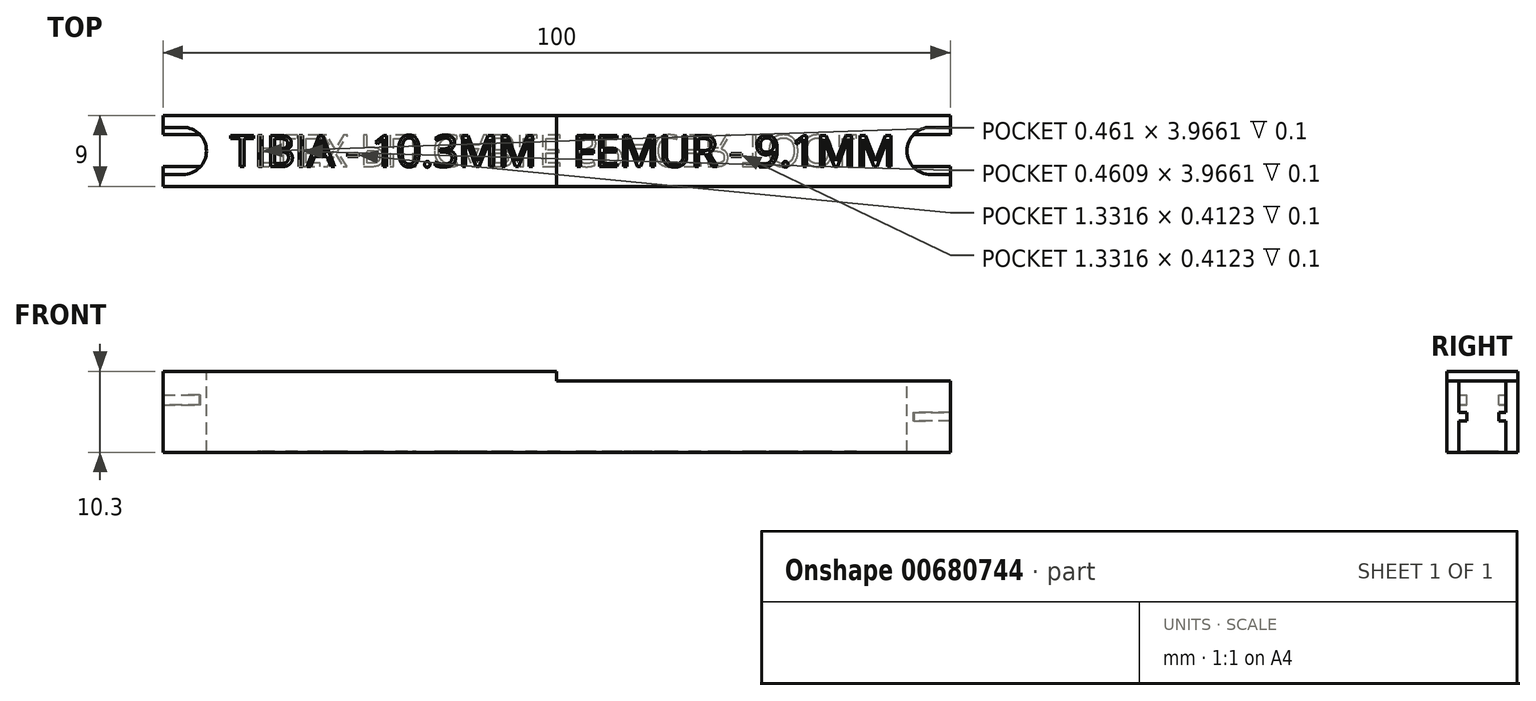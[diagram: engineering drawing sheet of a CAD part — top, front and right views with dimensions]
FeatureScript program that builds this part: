
annotation { "Feature Type Name" : "Feature", "Feature Type Description" : "" }
export const myFeature = defineFeature(function(context is Context, id is Id, definition is map)
    precondition{}
    {
        {
            var Q0;
            Q0=qCreatedBy(makeId("Front.planeOp"),FACE);
            var sketch = newSketch(context, id + "F0", { "sketchPlane" : qUnion([Q0])});
            skLineSegment(sketch, "E0.bottom", {"start": v(0, 0) * mm, "end": v(50, 0) * mm});
            skLineSegment(sketch, "E0.top", {"start": v(0, 10.3) * mm, "end": v(50, 10.3) * mm});
            skLineSegment(sketch, "E0.left", {"start": v(0, 0) * mm, "end": v(0, 10.3) * mm});
            skLineSegment(sketch, "E0.right", {"start": v(50, 9.1) * mm, "end": v(50, 10.3) * mm});
            skLineSegment(sketch, "E1.bottom", {"start": v(50, 0) * mm, "end": v(100, 0) * mm});
            skLineSegment(sketch, "E1.top", {"start": v(50, 9.1) * mm, "end": v(100, 9.1) * mm});
            skLineSegment(sketch, "E1.right", {"start": v(100, 0) * mm, "end": v(100, 9.1) * mm});
            skSolve(sketch);
        }
        {
            var Q0;
            Q0 = qSketchRegion(id + "F0", true);
            extrude(context, id + "F1", {"entities" : qUnion([Q0]), "depth" : 9 * mm, "offsetDistance" : 25 * mm});
        }
        {
            var Q0;
            Q0=makeQuery(id+"F1.opExtrude","SWEPT_FACE",FACE,{"disambiguationData":[OSD([sQuery(id+"F0.wireOp",EDGE,"E0.top")])]});
            var sketch = newSketch(context, id + "F2", { "sketchPlane" : qUnion([Q0])});
            skLineSegment(sketch, "E2.top", {"start": v(0, -1.5) * mm, "end": v(2.5, -1.5) * mm});
            skLineSegment(sketch, "E2.left", {"start": v(0, -4.5) * mm, "end": v(0, -1.5) * mm});
            skLineSegment(sketch, "E3.top", {"start": v(0, -7.5) * mm, "end": v(2.5, -7.5) * mm});
            skLineSegment(sketch, "E3.left", {"start": v(0, -4.5) * mm, "end": v(0, -7.5) * mm});
            skArc(sketch, "E4", {"start": v(2.5, -7.5) * mm, "mid": v(5.5, -4.5) * mm, "end": v(2.5, -1.5) * mm});
            skSolve(sketch);
        }
        {
            var Q0;
            Q0=makeQuery(id+"F1.opExtrude","SWEPT_FACE",FACE,{"disambiguationData":[OSD([sQuery(id+"F0.wireOp",EDGE,"E1.top")])]});
            var sketch = newSketch(context, id + "F3", { "sketchPlane" : qUnion([Q0])});
            skLineSegment(sketch, "E5.top", {"start": v(100, -1.5) * mm, "end": v(97.5, -1.5) * mm});
            skLineSegment(sketch, "E5.left", {"start": v(100, -4.5) * mm, "end": v(100, -1.5) * mm});
            skLineSegment(sketch, "E6.top", {"start": v(100, -7.5) * mm, "end": v(97.5, -7.5) * mm});
            skLineSegment(sketch, "E6.left", {"start": v(100, -4.5) * mm, "end": v(100, -7.5) * mm});
            skArc(sketch, "E7", {"start": v(97.5, -1.5) * mm, "mid": v(94.5, -4.5) * mm, "end": v(97.5, -7.5) * mm});
            skSolve(sketch);
        }
        {
            var Q0;
            Q0 = qSketchRegion(id + "F2", true);
            extrude(context, id + "F4", {"entities" : qUnion([Q0]), "operationType" : NewBodyOperationType.REMOVE, "oppositeDirection" : true, "depth" : 3 * mm, "offsetDistance" : 25 * mm});
        }
        {
            var Q0;
            Q0 = qSketchRegion(id + "F3", true);
            extrude(context, id + "F5", {"entities" : qUnion([Q0]), "operationType" : NewBodyOperationType.REMOVE, "oppositeDirection" : true, "depth" : 4 * mm, "offsetDistance" : 25 * mm});
        }
        {
            var Q0;
            Q0=makeQuery(id+"F1.opExtrude","SWEPT_FACE",FACE,{"disambiguationData":[OSD([sQuery(id+"F0.wireOp",EDGE,"E0.bottom"),sQuery(id+"F0.wireOp",EDGE,"E1.bottom")])]});
            var sketch = newSketch(context, id + "F6", { "sketchPlane" : qUnion([Q0])});
            skLineSegment(sketch, "E8.top", {"start": v(0, 7.5) * mm, "end": v(2.5, 7.5) * mm});
            skLineSegment(sketch, "E8.left", {"start": v(0, 4.5) * mm, "end": v(0, 7.5) * mm});
            skLineSegment(sketch, "E9.top", {"start": v(0, 1.5) * mm, "end": v(2.5, 1.5) * mm});
            skLineSegment(sketch, "E9.left", {"start": v(0, 4.5) * mm, "end": v(0, 1.5) * mm});
            skArc(sketch, "E10", {"start": v(2.5, 1.5) * mm, "mid": v(5.5, 4.5) * mm, "end": v(2.5, 7.5) * mm});
            skSolve(sketch);
        }
        {
            var Q0;
            Q0 = qSketchRegion(id + "F6", true);
            extrude(context, id + "F7", {"entities" : qUnion([Q0]), "operationType" : NewBodyOperationType.REMOVE, "oppositeDirection" : true, "depth" : 6 * mm, "offsetDistance" : 25 * mm});
        }
        {
            var Q0;
            Q0=makeQuery(id+"F1.opExtrude","SWEPT_FACE",FACE,{"disambiguationData":[OSD([sQuery(id+"F0.wireOp",EDGE,"E0.bottom"),sQuery(id+"F0.wireOp",EDGE,"E1.bottom")])]});
            var sketch = newSketch(context, id + "F8", { "sketchPlane" : qUnion([Q0])});
            skLineSegment(sketch, "E11.top", {"start": v(100, 7.5) * mm, "end": v(97.5, 7.5) * mm});
            skLineSegment(sketch, "E11.left", {"start": v(100, 4.5) * mm, "end": v(100, 7.5) * mm});
            skLineSegment(sketch, "E12.top", {"start": v(100, 1.5) * mm, "end": v(97.5, 1.5) * mm});
            skLineSegment(sketch, "E12.left", {"start": v(100, 4.5) * mm, "end": v(100, 1.5) * mm});
            skArc(sketch, "E13", {"start": v(97.5, 7.5) * mm, "mid": v(94.5, 4.5) * mm, "end": v(97.5, 1.5) * mm});
            skSolve(sketch);
        }
        {
            var Q0;
            Q0 = qSketchRegion(id + "F8", true);
            extrude(context, id + "F9", {"entities" : qUnion([Q0]), "operationType" : NewBodyOperationType.REMOVE, "oppositeDirection" : true, "depth" : 4 * mm, "offsetDistance" : 25 * mm});
        }
        {
            var Q0;
            Q0=makeQuery(id+"F4.boolean.opBoolean","COPY",FACE,{"derivedFrom":makeQuery(id+"F4.opExtrude","CAP_FACE",FACE,{"disambiguationData":[OSD([sQuery(id+"F2.wireOp",EDGE,"E2.top"),sQuery(id+"F2.wireOp",EDGE,"E2.left"),sQuery(id+"F2.wireOp",EDGE,"E3.top"),sQuery(id+"F2.wireOp",EDGE,"E3.left"),sQuery(id+"F2.wireOp",EDGE,"E4")])],"isStart":false})});
            var sketch = newSketch(context, id + "F10", { "sketchPlane" : qUnion([Q0])});
            skLineSegment(sketch, "E14", {"start": v(0, -6.5) * mm, "end": v(4.74, -6.5) * mm});
            skLineSegment(sketch, "E15", {"start": v(0, -2.4) * mm, "end": v(4.64, -2.4) * mm});
            skLineSegment(sketch, "E16", {"start": v(0, -2.4) * mm, "end": v(0, -6.5) * mm});
            skArc(sketch, "E17", {"start": v(4.74, -6.5) * mm, "mid": v(5.5, -4.43) * mm, "end": v(4.64, -2.4) * mm});
            skSolve(sketch);
        }
        {
            var Q0;
            Q0 = qSketchRegion(id + "F10", true);
            extrude(context, id + "F11", {"entities" : qUnion([Q0]), "operationType" : NewBodyOperationType.REMOVE, "oppositeDirection" : true, "depth" : 2 * mm, "offsetDistance" : 25 * mm});
        }
        {
            var Q0;
            Q0=makeQuery(id+"F9.boolean.opBoolean","COPY",FACE,{"derivedFrom":makeQuery(id+"F9.opExtrude","CAP_FACE",FACE,{"disambiguationData":[OSD([sQuery(id+"F8.wireOp",EDGE,"E11.top"),sQuery(id+"F8.wireOp",EDGE,"E11.left"),sQuery(id+"F8.wireOp",EDGE,"E12.top"),sQuery(id+"F8.wireOp",EDGE,"E12.left"),sQuery(id+"F8.wireOp",EDGE,"E13")])],"isStart":false})});
            var sketch = newSketch(context, id + "F12", { "sketchPlane" : qUnion([Q0])});
            skLineSegment(sketch, "E18", {"start": v(100, 6.5) * mm, "end": v(95.26, 6.5) * mm});
            skLineSegment(sketch, "E19", {"start": v(100, 2.4) * mm, "end": v(95.36, 2.4) * mm});
            skLineSegment(sketch, "E20", {"start": v(100, 2.4) * mm, "end": v(100, 6.5) * mm});
            skArc(sketch, "E21", {"start": v(95.26, 6.5) * mm, "mid": v(94.5, 4.43) * mm, "end": v(95.36, 2.4) * mm});
            skSolve(sketch);
        }
        {
            var Q0;
            Q0 = qSketchRegion(id + "F12", true);
            extrude(context, id + "F13", {"entities" : qUnion([Q0]), "operationType" : NewBodyOperationType.REMOVE, "oppositeDirection" : true, "depth" : 2 * mm, "offsetDistance" : 25 * mm});
        }
        {
            var Q0;
            Q0=makeQuery(id+"F1.opExtrude","SWEPT_FACE",FACE,{"disambiguationData":[OSD([sQuery(id+"F0.wireOp",EDGE,"E0.top")])]});
            var sketch = newSketch(context, id + "F14", { "sketchPlane" : qUnion([Q0])});
            skLineSegment(sketch, "E22", {"start": v(8.5, 0) * mm, "end": v(8.5, -9) * mm, "construction": true});
            skLineSegment(sketch, "E23", {"start": v(8.5, -2.5) * mm, "end": v(47.32, -2.5) * mm, "construction": true});
            skLineSegment(sketch, "E24", {"start": v(8.5, -6.5) * mm, "end": v(47.32, -6.5) * mm, "construction": true});
            skText(sketch, "E25", { "text": "TIBIA - 10.3MM", "fontName": "OpenSans-Regular.ttf"});
            const initialGuessF14  = {"E25": [0.0085, -0.0065, 1, 0, 0.004]};
            skSetInitialGuess(sketch, initialGuessF14);
            skSolve(sketch);
        }
        {
            var Q0;
            Q0=makeQuery(id+"F1.opExtrude","SWEPT_FACE",FACE,{"disambiguationData":[OSD([sQuery(id+"F0.wireOp",EDGE,"E1.top")])]});
            var sketch = newSketch(context, id + "F15", { "sketchPlane" : qUnion([Q0])});
            skLineSegment(sketch, "E26", {"start": v(53.7, -2.5) * mm, "end": v(92.8, -2.5) * mm, "construction": true});
            skLineSegment(sketch, "E27", {"start": v(53.7, -6.5) * mm, "end": v(92.8, -6.5) * mm, "construction": true});
            skText(sketch, "E28", { "text": "FEMUR - 9.1MM", "fontName": "OpenSans-Regular.ttf"});
            const initialGuessF15  = {"E28": [0.052, -0.0065, 1, 0, 0.004]};
            skSetInitialGuess(sketch, initialGuessF15);
            skSolve(sketch);
        }
        {
            var Q0;
            Q0 = qSketchRegion(id + "F14", true);
            extrude(context, id + "F16", {"entities" : qUnion([Q0]), "operationType" : NewBodyOperationType.REMOVE, "oppositeDirection" : true, "depth" : 0.1 * mm, "offsetDistance" : 25 * mm});
        }
        {
            var Q0;
            Q0 = qSketchRegion(id + "F15", true);
            extrude(context, id + "F17", {"entities" : qUnion([Q0]), "operationType" : NewBodyOperationType.REMOVE, "oppositeDirection" : true, "depth" : 0.1 * mm, "offsetDistance" : 25 * mm});
        }
        {
            var Q0;
            Q0=makeQuery(id+"F1.opExtrude","SWEPT_FACE",FACE,{"disambiguationData":[OSD([sQuery(id+"F0.wireOp",EDGE,"E0.bottom"),sQuery(id+"F0.wireOp",EDGE,"E1.bottom")])]});
            var sketch = newSketch(context, id + "F18", { "sketchPlane" : qUnion([Q0])});
            skLineSegment(sketch, "E29", {"start": v(7.24, 6.5) * mm, "end": v(93.12, 6.5) * mm, "construction": true});
            skLineSegment(sketch, "E30", {"start": v(7.24, 2.5) * mm, "end": v(93.22, 2.5) * mm, "construction": true});
            skLineSegment(sketch, "E31", {"start": v(11.43, 9) * mm, "end": v(11.43, 0) * mm, "construction": true});
            skText(sketch, "E32", { "text": "FLEX PLI CABLE SPACER TOOL", "fontName": "OpenSans-Regular.ttf"});
            const initialGuessF18  = {"E32": [0.01143, 0.0025, 1, 0, 0.004]};
            skSetInitialGuess(sketch, initialGuessF18);
            skSolve(sketch);
        }
        {
            var Q0;
            Q0 = qSketchRegion(id + "F18", true);
            extrude(context, id + "F19", {"entities" : qUnion([Q0]), "operationType" : NewBodyOperationType.REMOVE, "oppositeDirection" : true, "depth" : 0.1 * mm, "offsetDistance" : 25 * mm});
        }
    });
